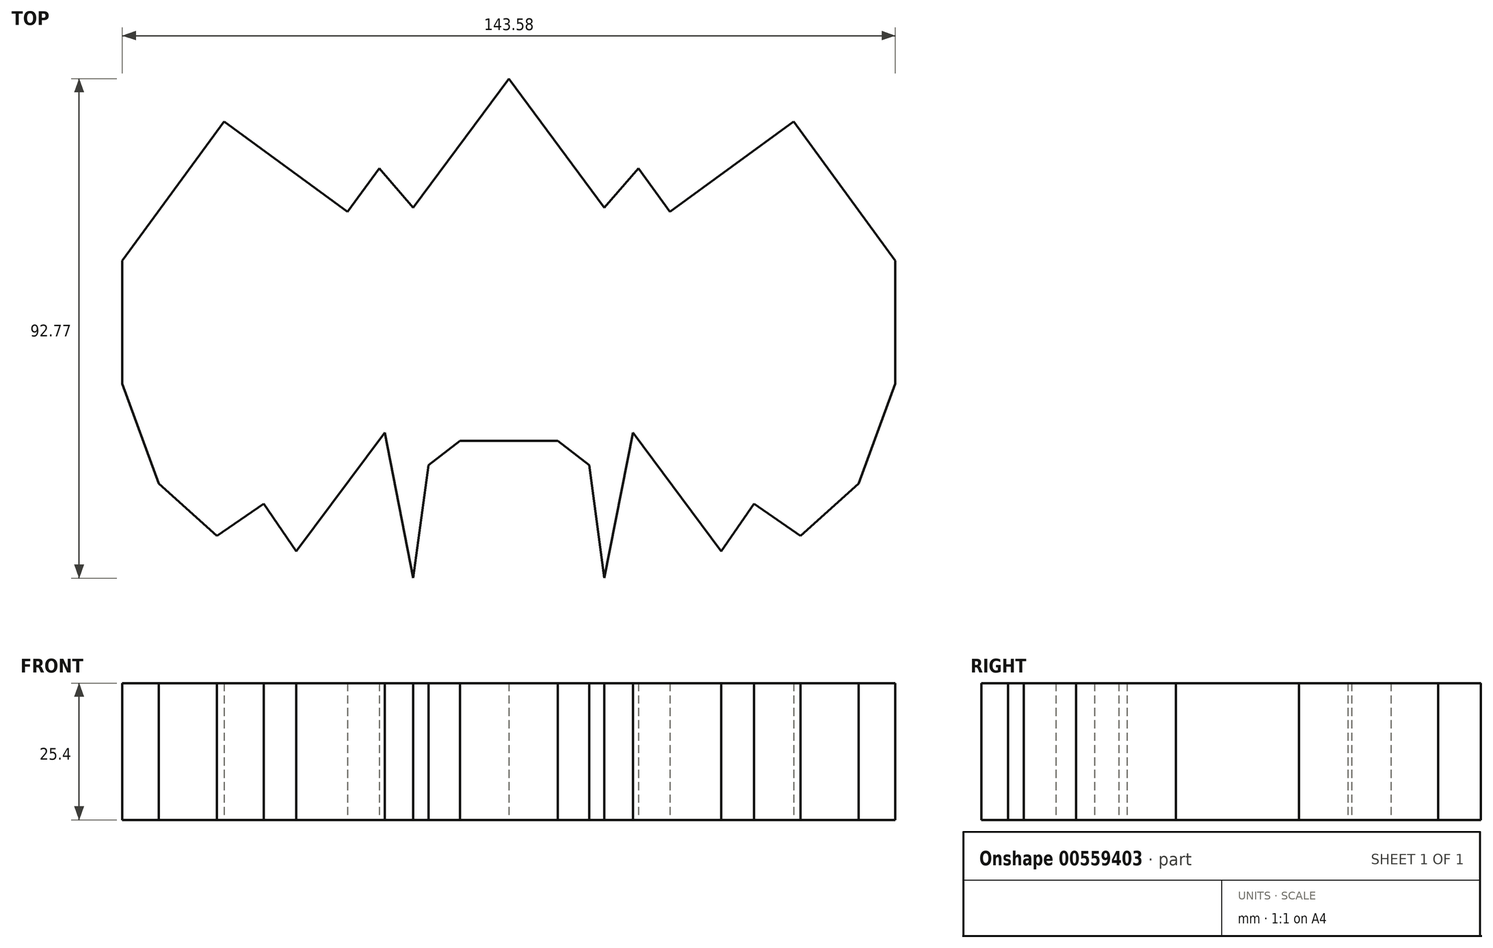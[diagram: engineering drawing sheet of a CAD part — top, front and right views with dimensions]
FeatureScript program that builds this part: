
annotation { "Feature Type Name" : "Feature", "Feature Type Description" : "" }
export const myFeature = defineFeature(function(context is Context, id is Id, definition is map)
    precondition{}
    {
        {
            var Q0;
            Q0=qCreatedBy(makeId("Top.planeOp"),FACE);
            var sketch = newSketch(context, id + "F0", { "sketchPlane" : qUnion([Q0])});
            skLineSegment(sketch, "E0", {"start": v(0, -25.41) * mm, "end": v(-9.07, -25.41) * mm});
            skLineSegment(sketch, "E1", {"start": v(-9.07, -25.41) * mm, "end": v(-14.93, -29.94) * mm});
            skLineSegment(sketch, "E2", {"start": v(-14.93, -29.94) * mm, "end": v(-23.05, -23.9) * mm});
            skLineSegment(sketch, "E3", {"start": v(-23.05, -23.9) * mm, "end": v(-39.47, -45.96) * mm});
            skLineSegment(sketch, "E4", {"start": v(-39.47, -45.96) * mm, "end": v(-45.53, -37.12) * mm});
            skLineSegment(sketch, "E5", {"start": v(-45.53, -37.12) * mm, "end": v(-54.19, -43.06) * mm});
            skLineSegment(sketch, "E6", {"start": v(-54.19, -43.06) * mm, "end": v(-65, -33.35) * mm});
            skLineSegment(sketch, "E7", {"start": v(-65, -33.35) * mm, "end": v(-71.8, -14.83) * mm});
            skLineSegment(sketch, "E8", {"start": v(-71.8, -14.83) * mm, "end": v(-71.8, 8.03) * mm});
            skLineSegment(sketch, "E9", {"start": v(-71.8, 8.03) * mm, "end": v(-52.9, 33.91) * mm});
            skLineSegment(sketch, "E10", {"start": v(-52.9, 33.91) * mm, "end": v(-29.93, 17.15) * mm});
            skLineSegment(sketch, "E11", {"start": v(-29.93, 17.15) * mm, "end": v(-24.08, 25.16) * mm});
            skLineSegment(sketch, "E12", {"start": v(-24.08, 25.16) * mm, "end": v(-17.76, 17.85) * mm});
            skLineSegment(sketch, "E13", {"start": v(-17.76, 17.85) * mm, "end": v(0, 41.85) * mm});
            skLineSegment(sketch, "E14", {"start": v(0, 41.85) * mm, "end": v(0, -25.41) * mm});
            skLineSegment(sketch, "E15", {"start": v(-14.93, -29.94) * mm, "end": v(-17.76, -50.92) * mm});
            skLineSegment(sketch, "E16", {"start": v(-17.76, -50.92) * mm, "end": v(-23.05, -23.9) * mm});
            skSolve(sketch);
        }
        {
            var Q0;
            Q0 = qSketchRegion(id + "F0", true);
            extrude(context, id + "F1", {"entities" : qUnion([Q0]), "depth" : 25.4 * mm, "offsetDistance" : 25.4 * mm});
        }
        {
            var Q0;
            Q0=makeQuery(id+"F1.opExtrude","SWEPT_BODY",BODY,{"disambiguationData":[OSD([sQuery(id+"F0.wireOp",EDGE,"E0"),sQuery(id+"F0.wireOp",EDGE,"E1"),sQuery(id+"F0.wireOp",EDGE,"E3"),sQuery(id+"F0.wireOp",EDGE,"E4"),sQuery(id+"F0.wireOp",EDGE,"E5"),sQuery(id+"F0.wireOp",EDGE,"E6"),sQuery(id+"F0.wireOp",EDGE,"E7"),sQuery(id+"F0.wireOp",EDGE,"E8"),sQuery(id+"F0.wireOp",EDGE,"E9"),sQuery(id+"F0.wireOp",EDGE,"E10"),sQuery(id+"F0.wireOp",EDGE,"E11"),sQuery(id+"F0.wireOp",EDGE,"E12"),sQuery(id+"F0.wireOp",EDGE,"E13"),sQuery(id+"F0.wireOp",EDGE,"E14"),sQuery(id+"F0.wireOp",EDGE,"E15"),sQuery(id+"F0.wireOp",EDGE,"E16")])]});
            var Q1;
            Q1=qCreatedBy(makeId("Right.planeOp"),FACE);
            mirror(context, id + "F2", {"operationType" : NewBodyOperationType.ADD, "entities" : qUnion([Q0]), "mirrorPlane" : qUnion([Q1])});
        }
    });
